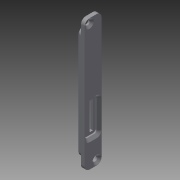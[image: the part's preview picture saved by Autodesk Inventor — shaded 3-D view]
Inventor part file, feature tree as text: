
AUTODESK INVENTOR PART (.ipt)
format: ipt  version: 2013 (Build 170138000, 138)  size: 167,424 bytes
history: native  units: in
note: dims shown in document units (in); Inventor stores cm internally (conversion verified against a paired STEP export)
features: extrude x3, sketch x3, chamfer x2
ambient origin geometry x8: Origin, YZ Plane, XZ Plane, XY Plane, X Axis, Y Axis, Z Axis, Center Point
bodies: Solid1 (feature_tree)
feature tree (8):
  extrude  "Extrusion1"  Depth=0.2677in
  chamfer  "Chamfer1"  Distance=0.0591in
  extrude  "Extrusion2"  Depth=0.0394in
  extrude  "Extrusion3"  Depth=0.0591in TaperAngle=0.0deg
  chamfer  "Chamfer2"  Distance=0.2677in
  sketch  "Sketch1"  dims[d0=2.0787in d1=0.2677in]
  sketch  "Sketch2"  dims[d2=0.0787in d3=0.0591in d4=0.0in]
  sketch  "Sketch3"  dims[d6=0.0315in d7=0.0787in d8=45.0deg d11=0.0394in d12=0.0591in d13=0.0in d14=0.2677in d15=1.7638in d16=0.0787in d17=0.0394in d18=0.0in d19=0.0394in d20=0.5118in d21=0.0394in d22=0.0394in d23=0.0394in d24=0.0394in d25=0.4134in d26=0.0394in d27=0.0787in d28=45.0deg d29=0.0394in d30=0.0984in d31=0.0394in d32=0.0512in d33=0.0394in d34=0.0394in d35=0.0787in d36=0.0039in d37=0.0039in]
